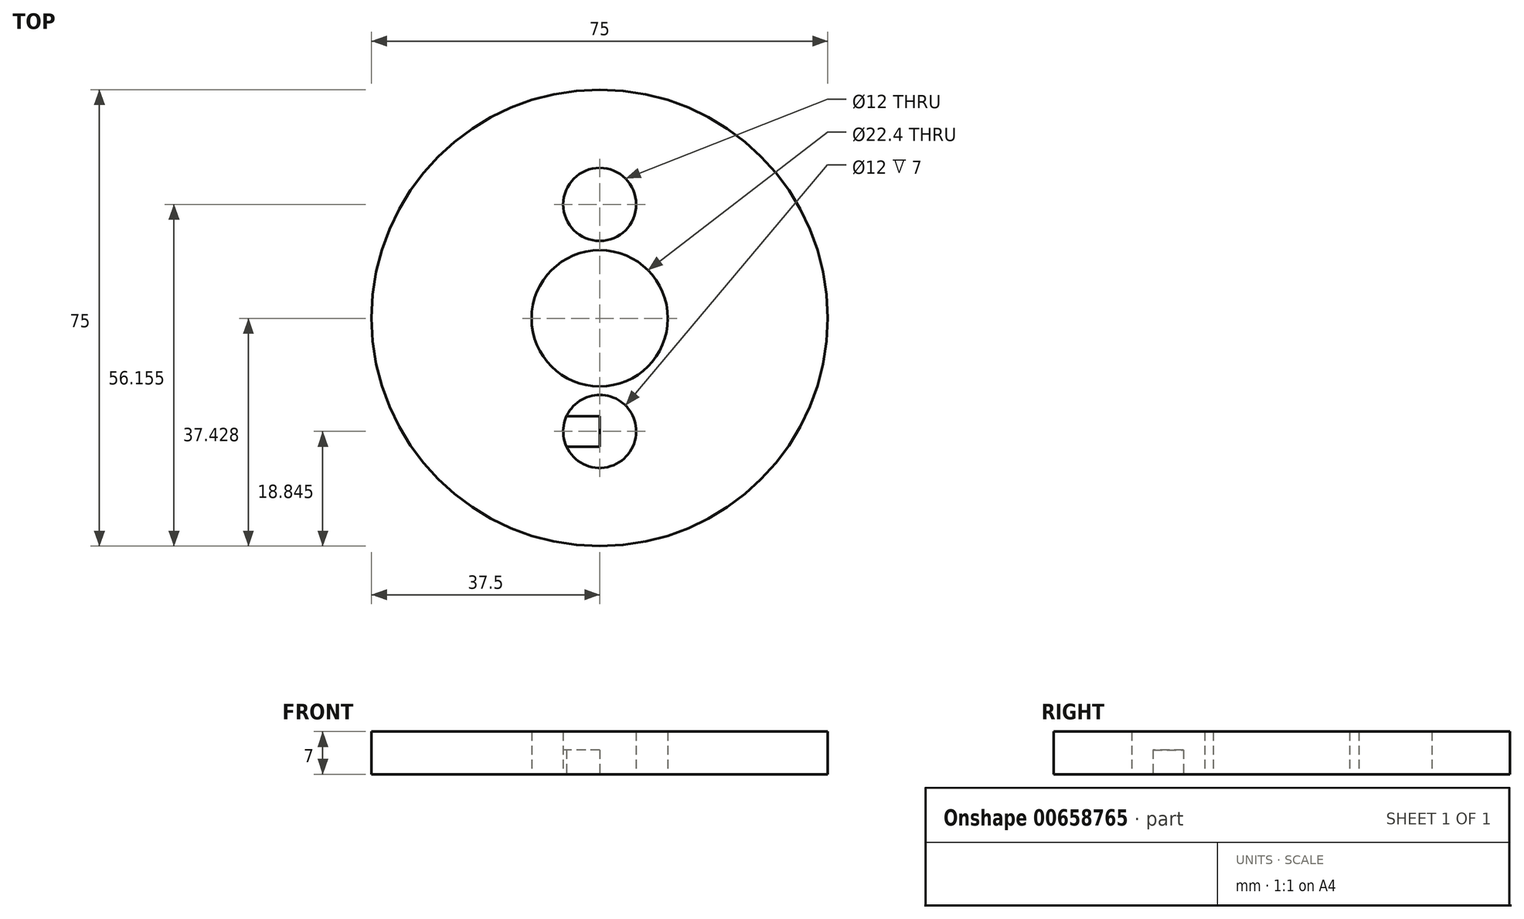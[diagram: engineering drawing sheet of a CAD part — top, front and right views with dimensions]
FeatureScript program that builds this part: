
annotation { "Feature Type Name" : "Feature", "Feature Type Description" : "" }
export const myFeature = defineFeature(function(context is Context, id is Id, definition is map)
    precondition{}
    {
        {
            var Q0;
            Q0=qCreatedBy(makeId("Top.planeOp"),FACE);
            var sketch = newSketch(context, id + "F0", { "sketchPlane" : qUnion([Q0])});
            skCircle(sketch, "E0", {"center": v(0, 0) * mm, "radius": 37.5 * mm});
            skLineSegment(sketch, "E1", {"start": v(0, 37.5) * mm, "end": v(0, -37.5) * mm, "construction": true});
            skLineSegment(sketch, "E2", {"start": v(-37.5, 0) * mm, "end": v(37.5, 0) * mm, "construction": true});
            skArc(sketch, "E3.1.0", {"start": v(0, 0.2) * mm, "mid": v(-18.85, -18.65) * mm, "end": v(0, -37.5) * mm});
            skArc(sketch, "E4.1.0", {"start": v(0, -0.07) * mm, "mid": v(18.85, 18.77) * mm, "end": v(0, 37.62) * mm});
            skPoint(sketch, "E4.center", {"position": v(0, 0.06) * mm});
            skCircle(sketch, "E5", {"center": v(0, -0.07) * mm, "radius": 11.2 * mm});
            skCircle(sketch, "E6", {"center": v(0, 18.65) * mm, "radius": 6 * mm});
            skCircle(sketch, "E7.MirrorC", {"center": v(0, -18.65) * mm, "radius": 6 * mm});
            skSolve(sketch);
        }
        {
            var Q0;
            Q0=makeQuery(id+"F0.imprint","IMPRINT",FACE,{"disambiguationData":[TD([[makeQuery(id+"F0.imprint","IMPRINT",EDGE,{"derivedFrom":sQuery(id+"F0.wireOp",EDGE,"E6")}),-1.0]])]});
            var Q1;
            Q1=makeQuery(id+"F0.imprint","IMPRINT",FACE,{"disambiguationData":[TD([[makeQuery(id+"F0.imprint","IMPRINT",EDGE,{"derivedFrom":sQuery(id+"F0.wireOp",EDGE,"E7.MirrorC")}),-1.0]])]});
            extrude(context, id + "F1", {"entities" : qUnion([Q0, Q1]), "depth" : 7 * mm, "offsetDistance" : 25 * mm});
        }
        {
            var Q0;
            Q0=qCreatedBy(makeId("Top.planeOp"),FACE);
            var sketch = newSketch(context, id + "F2", { "sketchPlane" : qUnion([Q0])});
            skCircle(sketch, "E8.0", {"center": v(0, 18.65) * mm, "radius": 6 * mm, "construction": true});
            skCircle(sketch, "E8.2", {"center": v(0, -18.65) * mm, "radius": 6 * mm, "construction": true});
            skLineSegment(sketch, "E9", {"start": v(0, -18.65) * mm, "end": v(-18.85, -18.65) * mm, "construction": true});
            skLineSegment(sketch, "E10.bottom", {"start": v(0, -21.15) * mm, "end": v(-18.85, -21.15) * mm});
            skLineSegment(sketch, "E10.top", {"start": v(0, -16.15) * mm, "end": v(-18.85, -16.15) * mm});
            skLineSegment(sketch, "E10.left", {"start": v(0, -21.15) * mm, "end": v(0, -16.15) * mm});
            skLineSegment(sketch, "E10.right", {"start": v(-18.85, -21.15) * mm, "end": v(-18.85, -16.15) * mm});
            skPoint(sketch, "E10.middle", {"position": v(-9.42, -18.65) * mm});
            skSolve(sketch);
        }
        {
            var Q0;
            Q0=makeQuery(id+"F2.imprint","IMPRINT",FACE,{"disambiguationData":[TD([[makeQuery(id+"F2.imprint","IMPRINT",EDGE,{"derivedFrom":sQuery(id+"F2.wireOp",EDGE,"E10.bottom")}),-1.0]])]});
            extrude(context, id + "F3", {"entities" : qUnion([Q0]), "operationType" : NewBodyOperationType.ADD, "depth" : 4 * mm, "offsetDistance" : 25 * mm});
        }
    });
